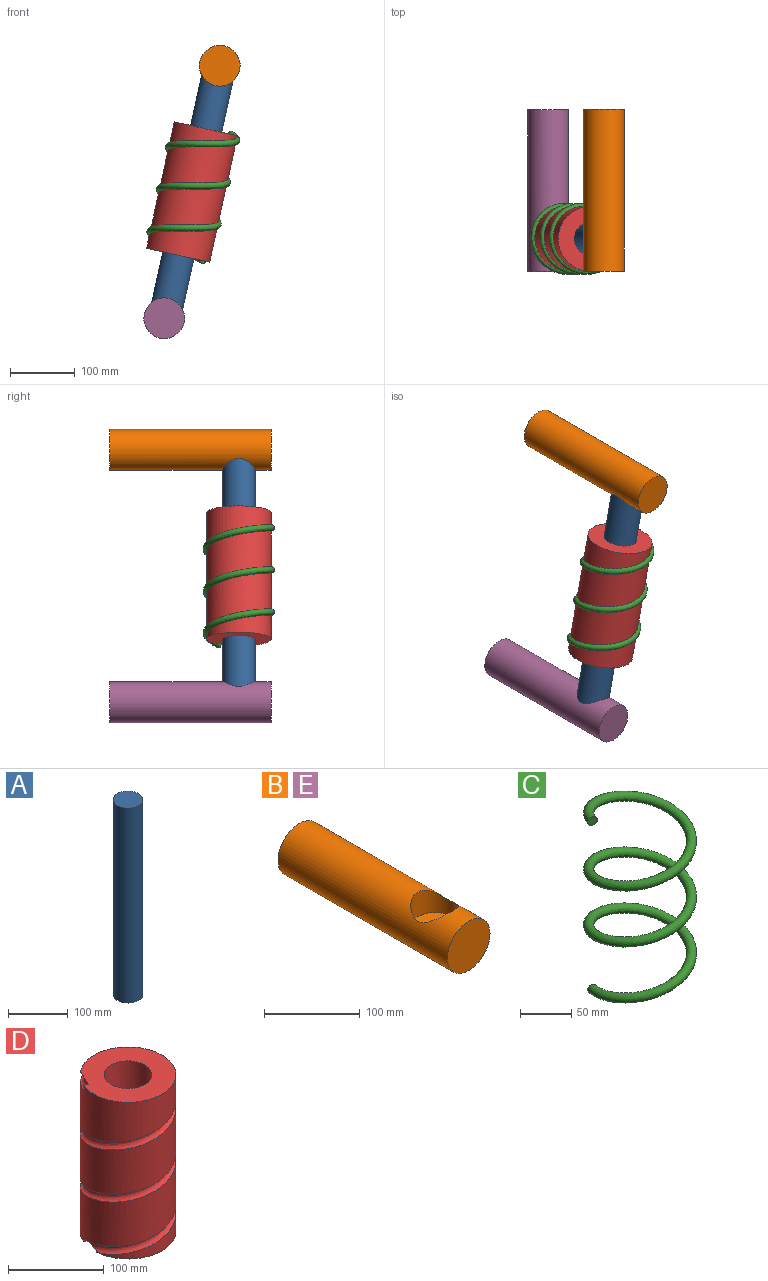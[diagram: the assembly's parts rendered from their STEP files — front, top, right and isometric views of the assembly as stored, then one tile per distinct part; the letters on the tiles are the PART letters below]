
ASSEMBLY  parts=5 mates=4
PART A: 3 faces, bbox 50x50x400 mm
  f0: cylinder r=25mm len=400mm, axis (0,0,-1), area 62831.9mm2, adj f1,f2
  f1: plane 50x50mm, normal (0,0,1), area 1963.5mm2, adj f0
  f2: plane 50x50mm, normal (0,0,-1), area 1963.5mm2, adj f0
PART B: 5 faces, bbox 62.9x250x62.9 mm
  f0: cylinder r=31.47mm len=250mm, axis (0,-1,0), area 47253.6mm2, adj f1,f2,f3
  f1: plane 62.94x62.94mm, normal (0,1,0), area 3110.9mm2, adj f0
  f2: plane 62.94x62.94mm, normal (0,-1,0), area 3110.9mm2, adj f0
  f3: cylinder r=25mm len=50mm, axis (0,0,-1), area 4031mm2, adj f0,f4
  f4: plane 50x50mm, normal (0,0,1), area 1963.5mm2, adj f3
PART C: 3 faces, bbox 111.2x112.7x220 mm
  f0: plane 10x9.24mm, normal (0.38,0.92,0), area 78.5mm2, adj f2
  f1: plane 10x9.24mm, normal (-0.38,-0.92,0), area 78.5mm2, adj f2
  f2: bspline ~220x112.65mm, area 29927.6mm2, adj f0,f1
PART D: 7 faces, bbox 111.2x112.7x220 mm
  f0: cylinder r=50mm len=200mm, axis (0,0,-1), area 53814.1mm2, adj f1,f2,f3,f4,f5
  f1: plane 100x100mm, normal (0,0,1), area 5801.9mm2, adj f0,f3,f5,f6
  f2: plane 100x99.85mm, normal (0,0,-1), area 5801.9mm2, adj f0,f4,f5,f6
  f3: plane 5x4.62mm, normal (0.38,0.92,0), area 19.6mm2, adj f0,f1,f5
  f4: plane 5x4.62mm, normal (-0.38,-0.92,0), area 19.6mm2, adj f0,f2,f5
  f5: bspline ~220x112.65mm, area 13830mm2, adj f0,f1,f2,f3,f4
  f6: cylinder r=25mm len=200mm, axis (0,0,-1), area 31415.9mm2, adj f1,f2
PART E: same geometry as B
PLACE A rot(axis=(0,1,0),12.4deg) t=(47.95,-6.17,188.86)mm
PLACE B rot(axis=(0,-1,0),167.6deg) t=(90.91,-6.17,384.19)mm fixed
PLACE C rot(axis=(0.13,-0.99,-0.01),167.7deg) t=(90.91,-6.17,384.19)mm
PLACE D rot(axis=(0.13,-0.99,-0.01),167.7deg) t=(90.91,-6.17,384.19)mm
PLACE E rot(axis=(0,1,0),12.4deg) t=(47.95,-6.17,188.86)mm fixed
MATE fastened C.f1 <-> D.f3  axis (0.6,-0.79,-0.13) through (86.59,24.4,180.36)mm
MATE fastened E.f3 <-> A.f0  axis (0.21,0,0.98) through (26.47,-6.17,91.2)mm
MATE revolute D.f0 <-> A.f0  axis (0.21,0,0.98) through (69.43,-6.17,286.53)mm
MATE fastened B.f3 <-> A.f0  axis (-0.21,0,-0.98) through (112.39,-6.17,481.86)mm
